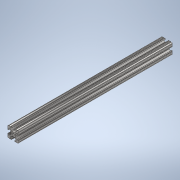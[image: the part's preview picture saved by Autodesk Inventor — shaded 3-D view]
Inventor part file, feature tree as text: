
AUTODESK INVENTOR PART (.ipt)
format: ipt  version: 2020 (Build 240168000, 168)  size: 239,104 bytes
history: native  units: in
note: dims shown in document units (in); Inventor stores cm internally (conversion verified against a paired STEP export)
features: extrude x1, sketch x1
ambient origin geometry x8: Origin, YZ Plane, XZ Plane, XY Plane, X Axis, Y Axis, Z Axis, Center Point
bodies: Solid1 (feature_tree)
feature tree (2):
  extrude  "Extrusion1"  [1 undecoded]
  sketch  "Sketch1"  dims[d0=14.0in d1=0.0in]
note: 1 required parameter value undecoded (feature->parameter linkage not recoverable at this tier; creation-order binding heuristic only, values carry confidence <= 0.55)
